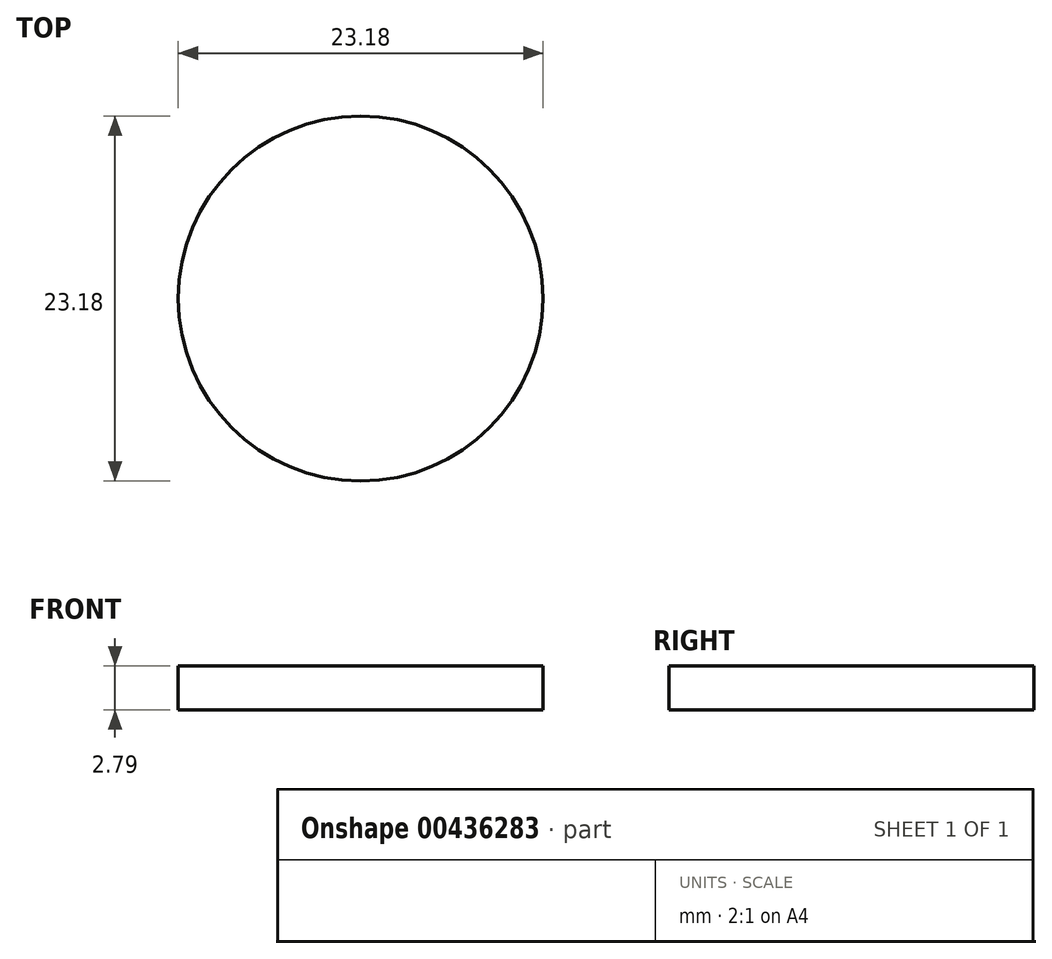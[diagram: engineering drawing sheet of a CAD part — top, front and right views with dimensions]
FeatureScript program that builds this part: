
annotation { "Feature Type Name" : "Feature", "Feature Type Description" : "" }
export const myFeature = defineFeature(function(context is Context, id is Id, definition is map)
    precondition{}
    {
        {
            var Q0;
            Q0=qCreatedBy(makeId("Top.planeOp"),FACE);
            var sketch = newSketch(context, id + "F0", { "sketchPlane" : qUnion([Q0])});
            skCircle(sketch, "E0", {"center": v(-7.12, 0) * mm, "radius": 11.59 * mm});
            skSolve(sketch);
        }
        {
            var Q0;
            Q0 = qSketchRegion(id + "F0", true);
            extrude(context, id + "F1", {"entities" : qUnion([Q0]), "depth" : 2.8 * mm, "offsetDistance" : 25.4 * mm});
        }
    });
